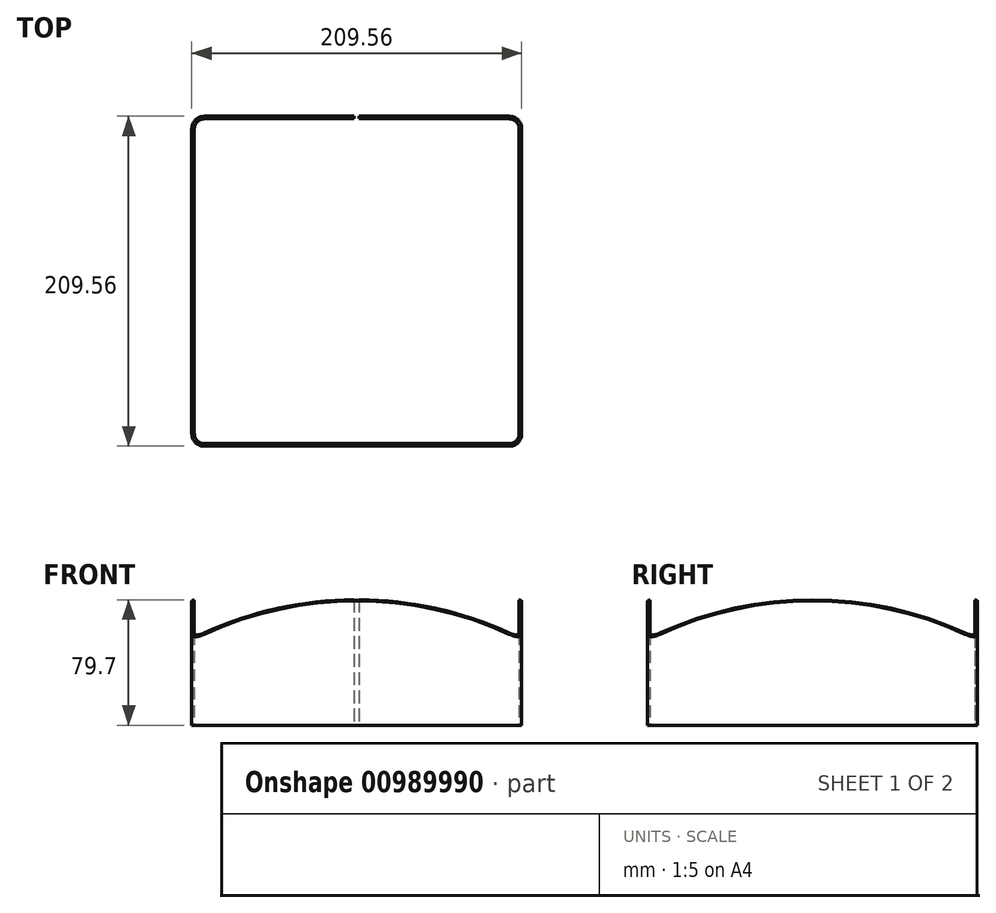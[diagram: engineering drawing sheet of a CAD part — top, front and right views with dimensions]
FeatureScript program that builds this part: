
annotation { "Feature Type Name" : "Feature", "Feature Type Description" : "" }
export const myFeature = defineFeature(function(context is Context, id is Id, definition is map)
    precondition{}
    {
        {
            var Q0;
            Q0=qCreatedBy(makeId("Top.planeOp"),FACE);
            var sketch = newSketch(context, id + "F0", { "sketchPlane" : qUnion([Q0])});
            skLineSegment(sketch, "E0.bottom", {"start": v(-104.78, 104.77) * mm, "end": v(104.78, 104.78) * mm});
            skLineSegment(sketch, "E0.top", {"start": v(-104.78, -104.78) * mm, "end": v(104.78, -104.77) * mm});
            skLineSegment(sketch, "E0.left", {"start": v(-104.78, 104.77) * mm, "end": v(-104.78, -104.78) * mm});
            skLineSegment(sketch, "E0.right", {"start": v(104.78, 104.78) * mm, "end": v(104.78, -104.77) * mm});
            skPoint(sketch, "E0.middle", {"position": v(0, 0) * mm});
            skLineSegment(sketch, "E1.0", {"start": v(-103.19, 103.19) * mm, "end": v(103.19, 103.19) * mm});
            skLineSegment(sketch, "E1.1", {"start": v(-103.19, 103.19) * mm, "end": v(-103.19, -103.19) * mm});
            skLineSegment(sketch, "E1.2", {"start": v(-103.19, -103.19) * mm, "end": v(103.19, -103.19) * mm});
            skLineSegment(sketch, "E1.3", {"start": v(103.19, 103.19) * mm, "end": v(103.19, -103.19) * mm});
            skLineSegment(sketch, "E2", {"start": v(93.66, -101.6) * mm, "end": v(103.19, -101.6) * mm});
            skCircle(sketch, "E3", {"center": v(-100.8, -99.22) * mm, "radius": 3.97 * mm});
            skLineSegment(sketch, "E4", {"start": v(-100.8, -99.22) * mm, "end": v(-104.78, -99.22) * mm});
            skLineSegment(sketch, "E5", {"start": v(-100.01, -100.01) * mm, "end": v(-142.13, -100.01) * mm});
            skLineSegment(sketch, "E6", {"start": v(-100.01, -135.43) * mm, "end": v(-100.01, -100.01) * mm});
            skLineSegment(sketch, "E7", {"start": v(-88.9, -140.4) * mm, "end": v(-88.9, -145.96) * mm});
            skCircle(sketch, "E8", {"center": v(-100.8, -99.22) * mm, "radius": 2.38 * mm});
            skLineSegment(sketch, "E9.bottom", {"start": v(-106.36, 106.36) * mm, "end": v(-100.4, 106.36) * mm});
            skLineSegment(sketch, "E9.top", {"start": v(-106.36, 100.4) * mm, "end": v(-100.4, 100.4) * mm});
            skLineSegment(sketch, "E9.left", {"start": v(-106.36, 106.36) * mm, "end": v(-106.36, 100.4) * mm});
            skLineSegment(sketch, "E9.right", {"start": v(-100.4, 106.36) * mm, "end": v(-100.4, 100.4) * mm});
            skLineSegment(sketch, "E10", {"start": v(-102.4, 102.4) * mm, "end": v(-102.4, 95.39) * mm, "construction": true});
            skLineSegment(sketch, "E11", {"start": v(-102.4, 102.4) * mm, "end": v(-97.37, 102.4) * mm, "construction": true});
            skPoint(sketch, "E12", {"position": v(-101.6, 101.1) * mm});
            skLineSegment(sketch, "E13.bottom", {"start": v(127, 127) * mm, "end": v(-127, 127) * mm});
            skLineSegment(sketch, "E13.top", {"start": v(127, -127) * mm, "end": v(-127, -127) * mm});
            skLineSegment(sketch, "E13.left", {"start": v(127, 127) * mm, "end": v(127, -127) * mm});
            skLineSegment(sketch, "E13.right", {"start": v(-127, 127) * mm, "end": v(-127, -127) * mm});
            skLineSegment(sketch, "E14.bottom", {"start": v(114.3, 114.3) * mm, "end": v(-114.3, 114.3) * mm});
            skLineSegment(sketch, "E14.top", {"start": v(114.3, -114.3) * mm, "end": v(-114.3, -114.3) * mm});
            skLineSegment(sketch, "E14.left", {"start": v(114.3, 114.3) * mm, "end": v(114.3, -114.3) * mm});
            skLineSegment(sketch, "E14.right", {"start": v(-114.3, 114.3) * mm, "end": v(-114.3, -114.3) * mm});
            skCircle(sketch, "E15", {"center": v(114.3, 90.47) * mm, "radius": 2.25 * mm});
            skCircle(sketch, "E16", {"center": v(90.47, 114.3) * mm, "radius": 2.25 * mm});
            skCircle(sketch, "E17", {"center": v(-114.3, 90.47) * mm, "radius": 2.25 * mm});
            skCircle(sketch, "E18", {"center": v(90.47, -114.3) * mm, "radius": 2.25 * mm});
            skCircle(sketch, "E19.0.1.0", {"center": v(114.3, 30.15) * mm, "radius": 2.25 * mm});
            skCircle(sketch, "E19.0.1.1", {"center": v(-114.3, 30.15) * mm, "radius": 2.25 * mm});
            skCircle(sketch, "E19.0.2.0", {"center": v(114.3, -30.18) * mm, "radius": 2.25 * mm});
            skCircle(sketch, "E19.0.2.1", {"center": v(-114.3, -30.18) * mm, "radius": 2.25 * mm});
            skCircle(sketch, "E19.0.3.0", {"center": v(114.3, -90.5) * mm, "radius": 2.25 * mm});
            skCircle(sketch, "E19.0.3.1", {"center": v(-114.3, -90.5) * mm, "radius": 2.25 * mm});
            skLineSegment(sketch, "E19.direction1", {"start": v(114.3, 90.47) * mm, "end": v(139.7, 90.47) * mm, "construction": true});
            skLineSegment(sketch, "E19.direction2", {"start": v(114.3, 90.47) * mm, "end": v(114.3, 30.15) * mm, "construction": true});
            skCircle(sketch, "E20.1.0.0", {"center": v(30.15, 114.3) * mm, "radius": 2.25 * mm});
            skCircle(sketch, "E20.1.0.1", {"center": v(30.15, -114.3) * mm, "radius": 2.25 * mm});
            skCircle(sketch, "E20.2.0.0", {"center": v(-30.18, 114.3) * mm, "radius": 2.25 * mm});
            skCircle(sketch, "E20.2.0.1", {"center": v(-30.18, -114.3) * mm, "radius": 2.25 * mm});
            skCircle(sketch, "E20.3.0.0", {"center": v(-90.5, 114.3) * mm, "radius": 2.25 * mm});
            skCircle(sketch, "E20.3.0.1", {"center": v(-90.5, -114.3) * mm, "radius": 2.25 * mm});
            skLineSegment(sketch, "E20.direction1", {"start": v(90.47, 114.3) * mm, "end": v(30.15, 114.3) * mm, "construction": true});
            skCircle(sketch, "E21", {"center": v(-114.3, 90.47) * mm, "radius": 6.35 * mm});
            skCircle(sketch, "E22", {"center": v(-90.5, 114.3) * mm, "radius": 6.35 * mm});
            skLineSegment(sketch, "E23.bottom", {"start": v(-120.65, 120.65) * mm, "end": v(120.65, 120.65) * mm});
            skLineSegment(sketch, "E23.top", {"start": v(-120.65, -120.65) * mm, "end": v(120.65, -120.65) * mm});
            skLineSegment(sketch, "E23.left", {"start": v(-120.65, 120.65) * mm, "end": v(-120.65, -120.65) * mm});
            skLineSegment(sketch, "E23.right", {"start": v(120.65, 120.65) * mm, "end": v(120.65, -120.65) * mm});
            skSolve(sketch);
        }
        {
            var Q0;
            Q0=qCreatedBy(makeId("Top.planeOp"),FACE);
            var sketch = newSketch(context, id + "F1", { "sketchPlane" : qUnion([Q0])});
            skLineSegment(sketch, "E24.0", {"start": v(-96.84, 103.19) * mm, "end": v(-1.59, 103.19) * mm});
            skLineSegment(sketch, "E24.1", {"start": v(103.19, 96.84) * mm, "end": v(103.19, -96.84) * mm});
            skLineSegment(sketch, "E24.2", {"start": v(-96.84, -103.19) * mm, "end": v(96.84, -103.19) * mm});
            skLineSegment(sketch, "E24.3", {"start": v(-103.19, 96.84) * mm, "end": v(-103.19, -96.84) * mm});
            skLineSegment(sketch, "E25", {"start": v(0, 0) * mm, "end": v(0, 114.03) * mm, "construction": true});
            skPoint(sketch, "E25.endSnap0", {"position": v(0, 103.19) * mm});
            skLineSegment(sketch, "E26", {"start": v(-1.59, 104.78) * mm, "end": v(-1.59, 103.19) * mm});
            skLineSegment(sketch, "E27", {"start": v(1.59, 104.78) * mm, "end": v(1.59, 103.19) * mm});
            skLineSegment(sketch, "E28.0", {"start": v(-96.84, 104.78) * mm, "end": v(-1.59, 104.78) * mm});
            skLineSegment(sketch, "E28.1", {"start": v(104.78, 96.84) * mm, "end": v(104.78, -96.84) * mm});
            skLineSegment(sketch, "E28.2", {"start": v(-96.84, -104.78) * mm, "end": v(96.84, -104.77) * mm});
            skLineSegment(sketch, "E28.3", {"start": v(-104.78, 96.84) * mm, "end": v(-104.78, -96.84) * mm});
            skLineSegment(sketch, "E29.trimOffspring", {"start": v(1.59, 104.78) * mm, "end": v(96.84, 104.78) * mm});
            skLineSegment(sketch, "E30.trimOffspring", {"start": v(1.59, 103.19) * mm, "end": v(96.84, 103.19) * mm});
            skPoint(sketch, "E31.visualSharp", {"position": v(-103.19, 103.19) * mm});
            skArc(sketch, "E31.filletArc", {"start": v(-96.84, 103.19) * mm, "mid": v(-101.33, 101.33) * mm, "end": v(-103.19, 96.84) * mm});
            skPoint(sketch, "E32.visualSharp", {"position": v(103.19, 103.19) * mm});
            skArc(sketch, "E32.filletArc", {"start": v(103.19, 96.84) * mm, "mid": v(101.33, 101.33) * mm, "end": v(96.84, 103.19) * mm});
            skPoint(sketch, "E33.visualSharp", {"position": v(103.19, -103.19) * mm});
            skArc(sketch, "E33.filletArc", {"start": v(96.84, -103.19) * mm, "mid": v(101.33, -101.33) * mm, "end": v(103.19, -96.84) * mm});
            skPoint(sketch, "E34.visualSharp", {"position": v(-103.19, -103.19) * mm});
            skArc(sketch, "E34.filletArc", {"start": v(-103.19, -96.84) * mm, "mid": v(-101.33, -101.33) * mm, "end": v(-96.84, -103.19) * mm});
            skPoint(sketch, "E35.visualSharp", {"position": v(-104.78, 104.77) * mm});
            skArc(sketch, "E35.filletArc", {"start": v(-96.84, 104.78) * mm, "mid": v(-102.45, 102.45) * mm, "end": v(-104.78, 96.84) * mm});
            skPoint(sketch, "E36.visualSharp", {"position": v(104.78, 104.78) * mm});
            skArc(sketch, "E36.filletArc", {"start": v(104.78, 96.84) * mm, "mid": v(102.45, 102.45) * mm, "end": v(96.84, 104.78) * mm});
            skPoint(sketch, "E37.visualSharp", {"position": v(104.78, -104.77) * mm});
            skArc(sketch, "E37.filletArc", {"start": v(96.84, -104.77) * mm, "mid": v(102.45, -102.45) * mm, "end": v(104.78, -96.84) * mm});
            skPoint(sketch, "E38.visualSharp", {"position": v(-104.78, -104.78) * mm});
            skArc(sketch, "E38.filletArc", {"start": v(-104.78, -96.84) * mm, "mid": v(-102.45, -102.45) * mm, "end": v(-96.84, -104.78) * mm});
            skSolve(sketch);
        }
        {
            var Q0;
            Q0=qSketchRegion(id+"F1",true);
            extrude(context, id + "F2", {"entities" : qUnion([Q0]), "depth" : 101.6 * mm, "offsetDistance" : 25.4 * mm});
        }
        {
            var Q0;
            Q0=qCreatedBy(makeId("Front.planeOp"),FACE);
            var sketch = newSketch(context, id + "F3", { "sketchPlane" : qUnion([Q0])});
            skLineSegment(sketch, "E39", {"start": v(0, 0) * mm, "end": v(0, 169.33) * mm});
            skCircle(sketch, "E40", {"center": v(0, -152.4) * mm, "radius": 254 * mm});
            skSolve(sketch);
        }
        {
            var Q0;
            Q0=qCreatedBy(makeId("Front.planeOp"),FACE);
            var sketch = newSketch(context, id + "F4", { "sketchPlane" : qUnion([Q0])});
            skArc(sketch, "E41.0", {"start": v(0, 101.6) * mm, "mid": v(-123.33, 69.65) * mm, "end": v(-215.63, -18.17) * mm});
            skPoint(sketch, "E42.orphan", {"position": v(0, 0) * mm});
            skPoint(sketch, "E43.orphan", {"position": v(0, 169.33) * mm});
            skLineSegment(sketch, "E44.0", {"start": v(0, 101.6) * mm, "end": v(0, 169.33) * mm});
            skLineSegment(sketch, "E45", {"start": v(0, 169.33) * mm, "end": v(-215.63, 169.33) * mm});
            skLineSegment(sketch, "E46", {"start": v(-215.63, 169.33) * mm, "end": v(-215.63, -18.17) * mm});
            skSolve(sketch);
        }
        {
            var Q0;
            Q0=qSketchRegion(id+"F4",true);
            var Q1;
            Q1=sQuery(id+"F4.wireOp",EDGE,"E44.0");
            revolve(context, id + "F5", {"operationType" : NewBodyOperationType.REMOVE, "surfaceOperationType" : NewSurfaceOperationType.NEW, "entities" : qUnion([Q0]), "axis" : qUnion([Q1]), "revolveType" : RevolveType.FULL, "oppositeDirection" : true});
        }
    });
